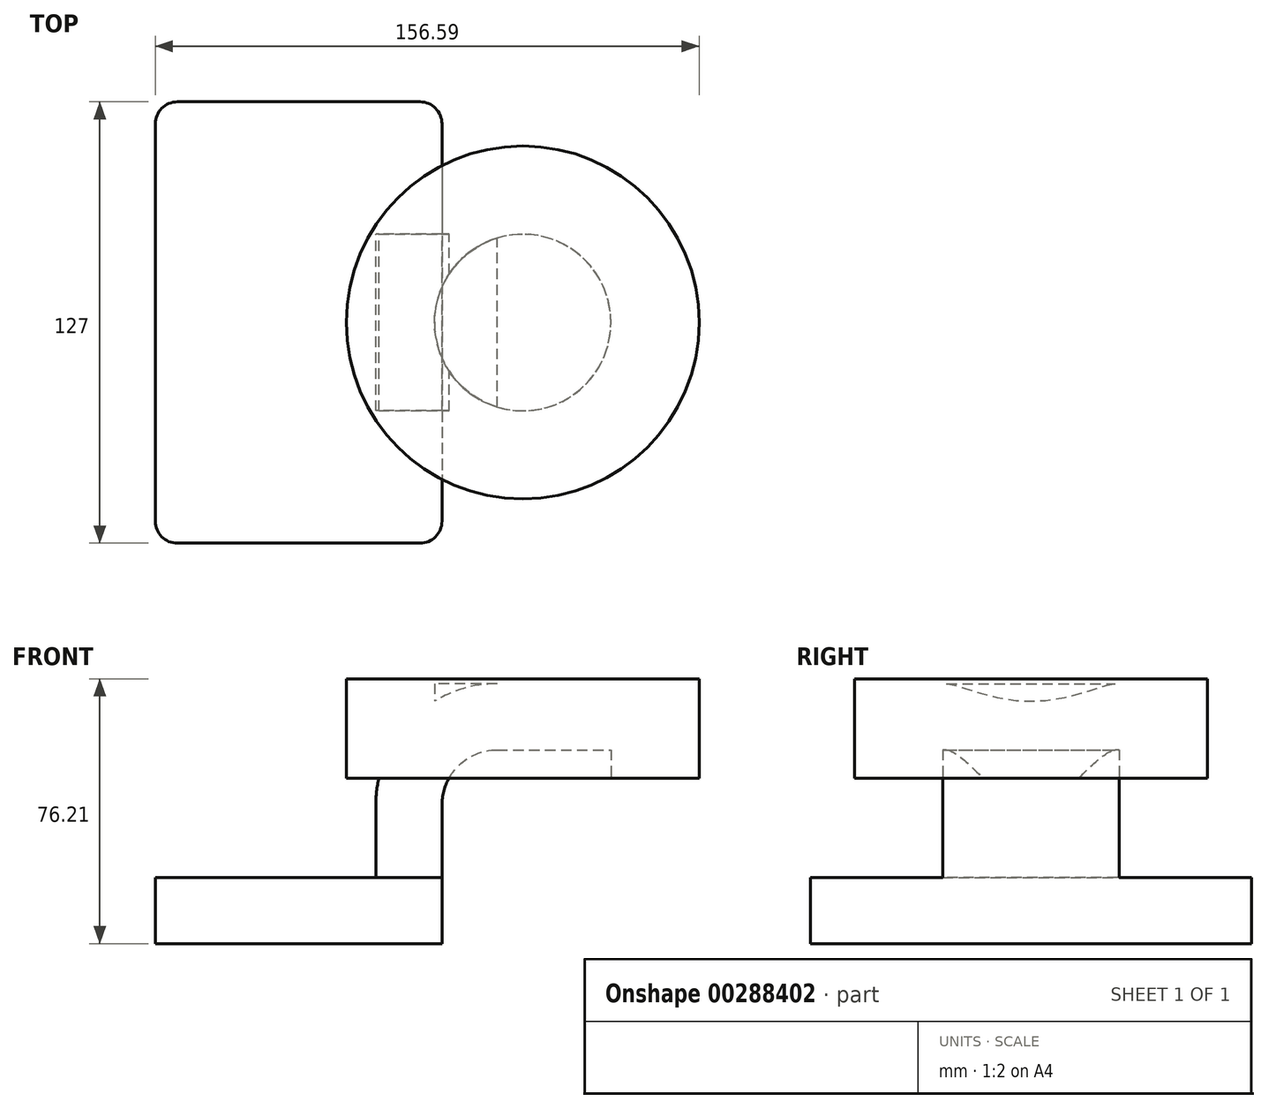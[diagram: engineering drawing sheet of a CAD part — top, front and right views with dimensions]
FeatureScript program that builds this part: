
annotation { "Feature Type Name" : "Feature", "Feature Type Description" : "" }
export const myFeature = defineFeature(function(context is Context, id is Id, definition is map)
    precondition{}
    {
        {
            var Q0;
            Q0=qCreatedBy(makeId("Front.planeOp"),FACE);
            var sketch = newSketch(context, id + "F0", { "sketchPlane" : qUnion([Q0])});
            skLineSegment(sketch, "E0.bottom", {"start": v(41.28, -9.52) * mm, "end": v(-41.27, -9.53) * mm});
            skLineSegment(sketch, "E0.top", {"start": v(41.27, 9.53) * mm, "end": v(-41.28, 9.53) * mm});
            skLineSegment(sketch, "E0.left", {"start": v(41.28, -9.52) * mm, "end": v(41.28, 9.53) * mm});
            skLineSegment(sketch, "E0.right", {"start": v(-41.27, -9.53) * mm, "end": v(-41.28, 9.53) * mm});
            skPoint(sketch, "E0.middle", {"position": v(0, 0) * mm});
            skLineSegment(sketch, "E1.bottom", {"start": v(64.52, 38.1) * mm, "end": v(115.32, 38.1) * mm});
            skLineSegment(sketch, "E1.top", {"start": v(64.52, 66.68) * mm, "end": v(115.32, 66.68) * mm});
            skLineSegment(sketch, "E1.left", {"start": v(64.52, 38.1) * mm, "end": v(64.52, 66.68) * mm});
            skLineSegment(sketch, "E1.right", {"start": v(115.32, 38.1) * mm, "end": v(115.32, 66.68) * mm});
            skPoint(sketch, "E1.middle", {"position": v(89.92, 52.39) * mm});
            skLineSegment(sketch, "E2", {"start": v(41.27, 9.53) * mm, "end": v(41.27, 30.33) * mm});
            skArc(sketch, "E3", {"start": v(41.27, 30.33) * mm, "mid": v(45.92, 41.55) * mm, "end": v(57.15, 46.2) * mm});
            skLineSegment(sketch, "E4", {"start": v(57.15, 46.2) * mm, "end": v(89.92, 46.2) * mm});
            skLineSegment(sketch, "E5.0", {"start": v(57.15, 65.25) * mm, "end": v(89.92, 65.25) * mm});
            skArc(sketch, "E5.1", {"start": v(22.23, 30.33) * mm, "mid": v(32.45, 55.02) * mm, "end": v(57.15, 65.25) * mm});
            skLineSegment(sketch, "E5.2", {"start": v(22.22, 9.53) * mm, "end": v(22.22, 30.33) * mm});
            skLineSegment(sketch, "E6", {"start": v(89.92, 38.1) * mm, "end": v(89.92, 65.25) * mm});
            skFitSpline(sketch, "E7", {"points": [v(-41.28, 9.53) * mm, v(57.15, 65.25) * mm], "startDerivative": vector(25.2, 15.8) * mm, "endDerivative": vector(182.3, -44.88) * mm});
            skSolve(sketch);
        }
        {
            var Q0;
            Q0=makeQuery(id+"F0.imprint","IMPRINT",FACE,{"disambiguationData":[TD([[makeQuery(id+"F0.imprint","IMPRINT",EDGE,{"derivedFrom":sQuery(id+"F0.wireOp",EDGE,"E0.bottom")}),-1.0]])]});
            extrude(context, id + "F1", {"entities" : qUnion([Q0]), "endBound" : BoundingType.SYMMETRIC, "oppositeDirection" : true, "depth" : 127 * mm});
        }
        {
            var Q0;
            {var subQ1=sQuery(id+"F0.wireOp",EDGE,"E2");Q0=makeQuery(id+"F0.imprint","IMPRINT",FACE,{"disambiguationData":[TD([[makeQuery(id+"F0.imprint","IMPRINT",EDGE,{"derivedFrom":subQ1}),1.0]])]});}
            var Q1;
            {var subQ0=sQuery(id+"F0.wireOp",EDGE,"E4");var subQ1=sQuery(id+"F0.wireOp",EDGE,"E1.left");var subQ2=makeQuery(id+"F0.imprint","INTERSECT",VERTEX,{"derivedFrom":[subQ1,subQ0]});Q1=makeQuery(id+"F0.imprint","IMPRINT",FACE,{"disambiguationData":[TD([[makeQuery(id+"F0.imprint","IMPRINT",EDGE,{"disambiguationData":[TD([[subQ2,-1.0]])],"derivedFrom":subQ1}),-1.0]])]});}
            extrude(context, id + "F2", {"entities" : qUnion([Q0, Q1]), "operationType" : NewBodyOperationType.ADD, "endBound" : BoundingType.SYMMETRIC, "depth" : 50.8 * mm});
        }
        {
            var Q0;
            Q0=makeQuery(id+"F0.imprint","IMPRINT",FACE,{"disambiguationData":[TD([[makeQuery(id+"F0.imprint","IMPRINT",EDGE,{"derivedFrom":sQuery(id+"F0.wireOp",EDGE,"E5.1")}),1.0]])]});
            extrude(context, id + "F3", {"entities" : qUnion([Q0]), "operationType" : NewBodyOperationType.ADD, "endBound" : BoundingType.SYMMETRIC, "depth" : 15.88 * mm});
        }
        {
            var Q0;
            {var subQ1=sQuery(id+"F0.wireOp",EDGE,"E1.top");Q0=makeQuery(id+"F0.imprint","IMPRINT",FACE,{"disambiguationData":[TD([[makeQuery(id+"F0.imprint","IMPRINT",EDGE,{"derivedFrom":subQ1}),-1.0]])]});}
            var Q1;
            Q1=sQuery(id+"F0.wireOp",EDGE,"E1.left");
            revolve(context, id + "F4", {"operationType" : NewBodyOperationType.ADD, "entities" : qUnion([Q0]), "axis" : qUnion([Q1]), "revolveType" : RevolveType.FULL});
        }
        {
            var Q0;
            Q0=makeQuery(id+"F1.opExtrude","CAP_EDGE",EDGE,{"disambiguationData":[OSD([sQuery(id+"F0.wireOp",EDGE,"E0.left")])],"isStart":true});
            var Q1;
            Q1=makeQuery(id+"F1.opExtrude","CAP_EDGE",EDGE,{"disambiguationData":[OSD([sQuery(id+"F0.wireOp",EDGE,"E0.right")])],"isStart":true});
            var Q2;
            Q2=makeQuery(id+"F1.opExtrude","CAP_EDGE",EDGE,{"disambiguationData":[OSD([sQuery(id+"F0.wireOp",EDGE,"E0.left")])],"isStart":false});
            var Q3;
            Q3=makeQuery(id+"F1.opExtrude","CAP_EDGE",EDGE,{"disambiguationData":[OSD([sQuery(id+"F0.wireOp",EDGE,"E0.right")])],"isStart":false});
            fillet(context, id + "F5", {"entities" : qUnion([Q0, Q1, Q2, Q3]), "radius" : 6.35 * mm, "tangentPropagation" : true, "allowEdgeOverflow" : false});
        }
    });
